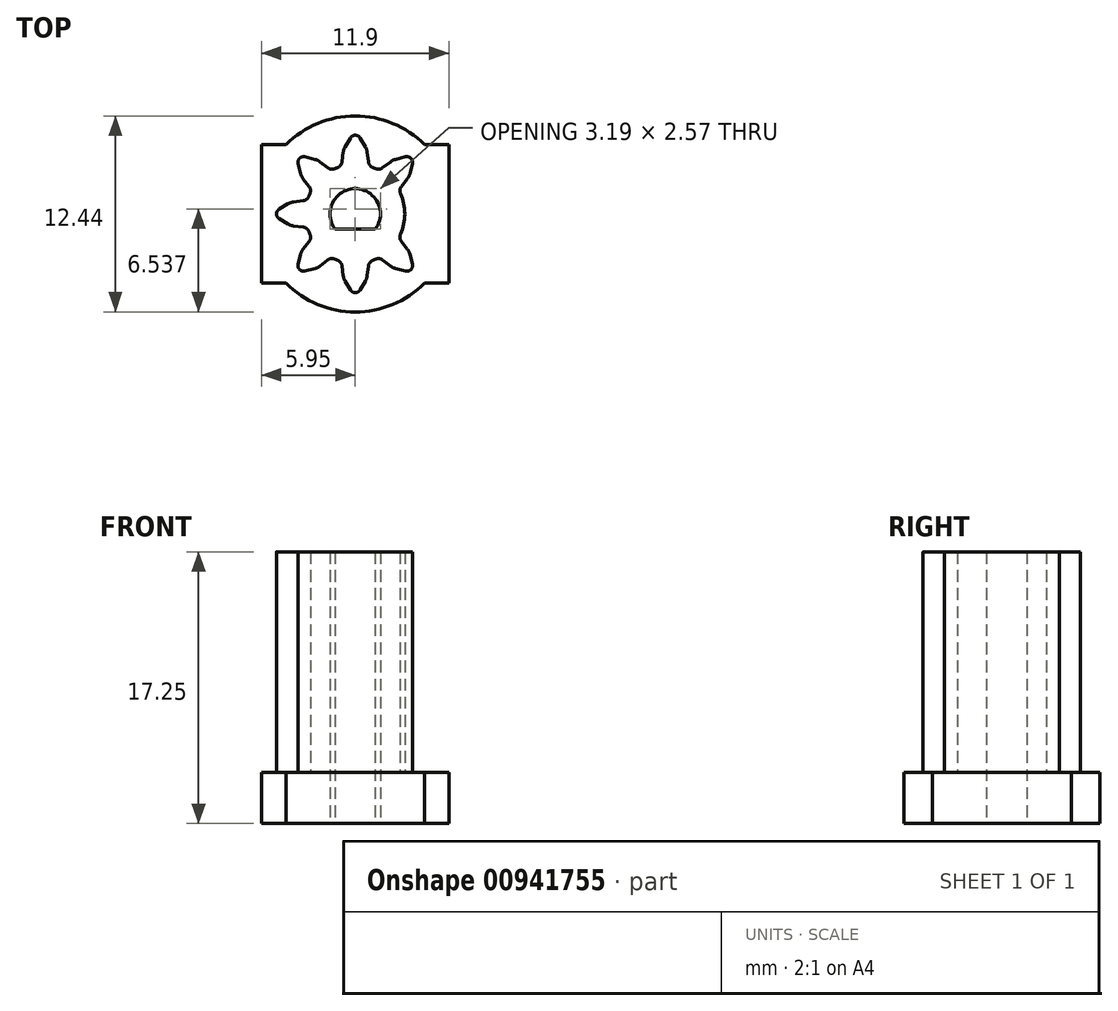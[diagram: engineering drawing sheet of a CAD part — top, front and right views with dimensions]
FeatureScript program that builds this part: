
annotation { "Feature Type Name" : "Feature", "Feature Type Description" : "" }
export const myFeature = defineFeature(function(context is Context, id is Id, definition is map)
    precondition{}
    {
        {
            var Q0;
            Q0=qCreatedBy(makeId("Top.planeOp"),FACE);
            var sketch = newSketch(context, id + "F0", { "sketchPlane" : qUnion([Q0])});
            skCircle(sketch, "E0", {"center": v(0, 0) * mm, "radius": 1.6 * mm});
            skCircle(sketch, "E1", {"center": v(0, 0) * mm, "radius": 2.55 * mm});
            skArc(sketch, "E2", {"start": v(-4.4, -4.4) * mm, "mid": v(0, -6.22) * mm, "end": v(4.4, -4.4) * mm});
            skCircle(sketch, "E3", {"center": v(0, 0) * mm, "radius": 3.15 * mm});
            skCircle(sketch, "E4", {"center": v(0, 0) * mm, "radius": 5 * mm});
            skLineSegment(sketch, "E5.bottom", {"start": v(-5.95, 4.4) * mm, "end": v(-4.4, 4.4) * mm});
            skLineSegment(sketch, "E5.top", {"start": v(-5.95, -4.4) * mm, "end": v(-4.4, -4.4) * mm});
            skLineSegment(sketch, "E5.left", {"start": v(-5.95, 4.4) * mm, "end": v(-5.95, -4.4) * mm});
            skLineSegment(sketch, "E5.right", {"start": v(5.95, 4.4) * mm, "end": v(5.95, -4.4) * mm});
            skArc(sketch, "E6.trimOffspring", {"start": v(4.4, 4.4) * mm, "mid": v(0, 6.22) * mm, "end": v(-4.4, 4.4) * mm});
            skLineSegment(sketch, "E7.trimOffspring", {"start": v(4.4, 4.4) * mm, "end": v(5.95, 4.4) * mm});
            skLineSegment(sketch, "E8.trimOffspring", {"start": v(4.4, -4.4) * mm, "end": v(5.95, -4.4) * mm});
            skLineSegment(sketch, "E9", {"start": v(0, 6.22) * mm, "end": v(0, -6.22) * mm, "construction": true});
            skLineSegment(sketch, "E10", {"start": v(-1.27, -0.97) * mm, "end": v(1.27, -0.97) * mm});
            skSolve(sketch);
        }
        {
            var Q0;
            Q0=makeQuery(id+"F0.imprint","IMPRINT",FACE,{"disambiguationData":[TD([[makeQuery(id+"F0.imprint","IMPRINT",EDGE,{"derivedFrom":sQuery(id+"F0.wireOp",EDGE,"E2")}),1.0]])]});
            var Q1;
            Q1=makeQuery(id+"F0.imprint","IMPRINT",FACE,{"disambiguationData":[TD([[makeQuery(id+"F0.imprint","IMPRINT",EDGE,{"derivedFrom":sQuery(id+"F0.wireOp",EDGE,"E3")}),-1.0]])]});
            var Q2;
            Q2=makeQuery(id+"F0.imprint","IMPRINT",FACE,{"disambiguationData":[TD([[makeQuery(id+"F0.imprint","IMPRINT",EDGE,{"derivedFrom":sQuery(id+"F0.wireOp",EDGE,"E0")}),-1.0]])]});
            var Q3;
            Q3=makeQuery(id+"F0.imprint","IMPRINT",FACE,{"disambiguationData":[TD([[makeQuery(id+"F0.imprint","IMPRINT",EDGE,{"derivedFrom":sQuery(id+"F0.wireOp",EDGE,"E1")}),-1.0]])]});
            var Q4;
            {var subQ0=sQuery(id+"F0.wireOp",EDGE,"Gm9W4LpN-Av9A-MbCA-gdo4-SThQoX5Y8GiM");Q4=makeQuery(id+"F0.imprint","IMPRINT",FACE,{"disambiguationData":[TD([[makeQuery(id+"F0.imprint","IMPRINT",EDGE,{"derivedFrom":subQ0}),-1.0]])]});}
            var Q5;
            {var subQ0=sQuery(id+"F0.wireOp",EDGE,"E10");Q5=makeQuery(id+"F0.imprint","IMPRINT",FACE,{"disambiguationData":[TD([[makeQuery(id+"F0.imprint","IMPRINT",EDGE,{"derivedFrom":subQ0}),-1.0]])]});}
            extrude(context, id + "F1", {"entities" : qUnion([Q0, Q1, Q2, Q3, Q4, Q5]), "depth" : 3.25 * mm, "offsetDistance" : 25 * mm});
        }
        {
            var Q0;
            Q0=makeQuery(id+"F1.opExtrude","CAP_FACE",FACE,{"disambiguationData":[OSD([sQuery(id+"F0.wireOp",EDGE,"E0"),sQuery(id+"F0.wireOp",EDGE,"E2"),sQuery(id+"F0.wireOp",EDGE,"E5.bottom"),sQuery(id+"F0.wireOp",EDGE,"E5.top"),sQuery(id+"F0.wireOp",EDGE,"E5.left"),sQuery(id+"F0.wireOp",EDGE,"E5.right"),sQuery(id+"F0.wireOp",EDGE,"E6.trimOffspring"),sQuery(id+"F0.wireOp",EDGE,"E7.trimOffspring"),sQuery(id+"F0.wireOp",EDGE,"E8.trimOffspring")])],"isStart":false});
            var sketch = newSketch(context, id + "F2", { "sketchPlane" : qUnion([Q0])});
            skCircle(sketch, "E11.0", {"center": v(0, 0) * mm, "radius": 5 * mm});
            skCircle(sketch, "E12.0", {"center": v(0, 0) * mm, "radius": 3.15 * mm});
            skCircle(sketch, "E13.0", {"center": v(0, 0) * mm, "radius": 2.55 * mm});
            skArc(sketch, "E14", {"start": v(4.83, -0.3) * mm, "mid": v(5, 0) * mm, "end": v(4.83, 0.3) * mm});
            skArc(sketch, "E15", {"start": v(3.31, -0.84) * mm, "mid": v(3.09, -0.93) * mm, "end": v(2.94, -1.13) * mm});
            skLineSegment(sketch, "E16", {"start": v(4.26, -0.64) * mm, "end": v(4.83, -0.3) * mm});
            skLineSegment(sketch, "E17", {"start": v(4.83, 0.3) * mm, "end": v(4.26, 0.64) * mm});
            skLineSegment(sketch, "E18", {"start": v(0, 0) * mm, "end": v(5.95, 0) * mm, "construction": true});
            skCircle(sketch, "E19.0", {"center": v(0, 0) * mm, "radius": 4.06 * mm, "construction": true});
            skArc(sketch, "E20", {"start": v(3.91, -0.76) * mm, "mid": v(4.1, -0.72) * mm, "end": v(4.26, -0.64) * mm});
            skLineSegment(sketch, "E21", {"start": v(3.91, -0.76) * mm, "end": v(3.31, -0.84) * mm});
            skArc(sketch, "E22.MirrorCS", {"start": v(3.91, 0.76) * mm, "mid": v(4.1, 0.72) * mm, "end": v(4.26, 0.64) * mm});
            skLineSegment(sketch, "E23.MirrorCS", {"start": v(3.91, 0.76) * mm, "end": v(3.31, 0.84) * mm});
            skArc(sketch, "E24.MirrorCS", {"start": v(3.31, 0.84) * mm, "mid": v(3.09, 0.93) * mm, "end": v(2.94, 1.13) * mm});
            skArc(sketch, "E25.1.0", {"start": v(1.75, -2.93) * mm, "mid": v(1.53, -2.84) * mm, "end": v(1.28, -2.88) * mm});
            skLineSegment(sketch, "E25.1.1", {"start": v(2.23, -3.3) * mm, "end": v(1.75, -2.93) * mm});
            skArc(sketch, "E25.1.2", {"start": v(2.23, -3.3) * mm, "mid": v(2.38, -3.4) * mm, "end": v(2.56, -3.47) * mm});
            skLineSegment(sketch, "E25.1.3", {"start": v(2.56, -3.47) * mm, "end": v(3.2, -3.63) * mm});
            skArc(sketch, "E25.1.4", {"start": v(3.2, -3.63) * mm, "mid": v(3.54, -3.54) * mm, "end": v(3.63, -3.2) * mm});
            skLineSegment(sketch, "E25.1.5", {"start": v(3.63, -3.2) * mm, "end": v(3.47, -2.56) * mm});
            skArc(sketch, "E25.1.6", {"start": v(3.3, -2.23) * mm, "mid": v(3.4, -2.38) * mm, "end": v(3.47, -2.56) * mm});
            skLineSegment(sketch, "E25.1.7", {"start": v(3.3, -2.23) * mm, "end": v(2.93, -1.75) * mm});
            skArc(sketch, "E25.1.8", {"start": v(2.93, -1.75) * mm, "mid": v(2.84, -1.53) * mm, "end": v(2.88, -1.28) * mm});
            skArc(sketch, "E25.2.0", {"start": v(-0.84, -3.31) * mm, "mid": v(-0.93, -3.09) * mm, "end": v(-1.12, -2.94) * mm});
            skLineSegment(sketch, "E25.2.1", {"start": v(-0.76, -3.91) * mm, "end": v(-0.84, -3.31) * mm});
            skArc(sketch, "E25.2.2", {"start": v(-0.76, -3.91) * mm, "mid": v(-0.72, -4.1) * mm, "end": v(-0.64, -4.26) * mm});
            skLineSegment(sketch, "E25.2.3", {"start": v(-0.64, -4.26) * mm, "end": v(-0.3, -4.83) * mm});
            skArc(sketch, "E25.2.4", {"start": v(-0.3, -4.83) * mm, "mid": v(0, -5) * mm, "end": v(0.3, -4.83) * mm});
            skLineSegment(sketch, "E25.2.5", {"start": v(0.3, -4.83) * mm, "end": v(0.64, -4.26) * mm});
            skArc(sketch, "E25.2.6", {"start": v(0.76, -3.91) * mm, "mid": v(0.72, -4.1) * mm, "end": v(0.64, -4.26) * mm});
            skLineSegment(sketch, "E25.2.7", {"start": v(0.76, -3.91) * mm, "end": v(0.84, -3.31) * mm});
            skArc(sketch, "E25.2.8", {"start": v(0.84, -3.31) * mm, "mid": v(0.93, -3.09) * mm, "end": v(1.13, -2.94) * mm});
            skArc(sketch, "E25.3.0", {"start": v(-2.93, -1.75) * mm, "mid": v(-2.84, -1.53) * mm, "end": v(-2.88, -1.28) * mm});
            skLineSegment(sketch, "E25.3.1", {"start": v(-3.3, -2.23) * mm, "end": v(-2.93, -1.75) * mm});
            skArc(sketch, "E25.3.2", {"start": v(-3.3, -2.23) * mm, "mid": v(-3.4, -2.38) * mm, "end": v(-3.47, -2.56) * mm});
            skLineSegment(sketch, "E25.3.3", {"start": v(-3.47, -2.56) * mm, "end": v(-3.63, -3.2) * mm});
            skArc(sketch, "E25.3.4", {"start": v(-3.63, -3.2) * mm, "mid": v(-3.54, -3.54) * mm, "end": v(-3.2, -3.63) * mm});
            skLineSegment(sketch, "E25.3.5", {"start": v(-3.2, -3.63) * mm, "end": v(-2.56, -3.47) * mm});
            skArc(sketch, "E25.3.6", {"start": v(-2.23, -3.3) * mm, "mid": v(-2.38, -3.4) * mm, "end": v(-2.56, -3.47) * mm});
            skLineSegment(sketch, "E25.3.7", {"start": v(-2.23, -3.3) * mm, "end": v(-1.75, -2.93) * mm});
            skArc(sketch, "E25.3.8", {"start": v(-1.75, -2.93) * mm, "mid": v(-1.53, -2.84) * mm, "end": v(-1.28, -2.88) * mm});
            skArc(sketch, "E25.4.0", {"start": v(-3.31, 0.84) * mm, "mid": v(-3.09, 0.93) * mm, "end": v(-2.94, 1.12) * mm});
            skLineSegment(sketch, "E25.4.1", {"start": v(-3.91, 0.76) * mm, "end": v(-3.31, 0.84) * mm});
            skArc(sketch, "E25.4.2", {"start": v(-3.91, 0.76) * mm, "mid": v(-4.1, 0.72) * mm, "end": v(-4.26, 0.64) * mm});
            skLineSegment(sketch, "E25.4.3", {"start": v(-4.26, 0.64) * mm, "end": v(-4.83, 0.3) * mm});
            skArc(sketch, "E25.4.4", {"start": v(-4.83, 0.3) * mm, "mid": v(-5, 0) * mm, "end": v(-4.83, -0.3) * mm});
            skLineSegment(sketch, "E25.4.5", {"start": v(-4.83, -0.3) * mm, "end": v(-4.26, -0.64) * mm});
            skArc(sketch, "E25.4.6", {"start": v(-3.91, -0.76) * mm, "mid": v(-4.1, -0.72) * mm, "end": v(-4.26, -0.64) * mm});
            skLineSegment(sketch, "E25.4.7", {"start": v(-3.91, -0.76) * mm, "end": v(-3.31, -0.84) * mm});
            skArc(sketch, "E25.4.8", {"start": v(-3.31, -0.84) * mm, "mid": v(-3.09, -0.93) * mm, "end": v(-2.94, -1.13) * mm});
            skArc(sketch, "E25.5.0", {"start": v(-1.75, 2.93) * mm, "mid": v(-1.53, 2.84) * mm, "end": v(-1.28, 2.88) * mm});
            skLineSegment(sketch, "E25.5.1", {"start": v(-2.23, 3.3) * mm, "end": v(-1.75, 2.93) * mm});
            skArc(sketch, "E25.5.2", {"start": v(-2.23, 3.3) * mm, "mid": v(-2.38, 3.4) * mm, "end": v(-2.56, 3.47) * mm});
            skLineSegment(sketch, "E25.5.3", {"start": v(-2.56, 3.47) * mm, "end": v(-3.2, 3.63) * mm});
            skArc(sketch, "E25.5.4", {"start": v(-3.2, 3.63) * mm, "mid": v(-3.54, 3.54) * mm, "end": v(-3.63, 3.2) * mm});
            skLineSegment(sketch, "E25.5.5", {"start": v(-3.63, 3.2) * mm, "end": v(-3.47, 2.56) * mm});
            skArc(sketch, "E25.5.6", {"start": v(-3.3, 2.23) * mm, "mid": v(-3.4, 2.38) * mm, "end": v(-3.47, 2.56) * mm});
            skLineSegment(sketch, "E25.5.7", {"start": v(-3.3, 2.23) * mm, "end": v(-2.93, 1.75) * mm});
            skArc(sketch, "E25.5.8", {"start": v(-2.93, 1.75) * mm, "mid": v(-2.84, 1.53) * mm, "end": v(-2.88, 1.28) * mm});
            skArc(sketch, "E25.6.0", {"start": v(0.84, 3.31) * mm, "mid": v(0.93, 3.09) * mm, "end": v(1.12, 2.94) * mm});
            skLineSegment(sketch, "E25.6.1", {"start": v(0.76, 3.91) * mm, "end": v(0.84, 3.31) * mm});
            skArc(sketch, "E25.6.2", {"start": v(0.76, 3.91) * mm, "mid": v(0.72, 4.1) * mm, "end": v(0.64, 4.26) * mm});
            skLineSegment(sketch, "E25.6.3", {"start": v(0.64, 4.26) * mm, "end": v(0.3, 4.83) * mm});
            skArc(sketch, "E25.6.4", {"start": v(0.3, 4.83) * mm, "mid": v(0, 5) * mm, "end": v(-0.3, 4.83) * mm});
            skLineSegment(sketch, "E25.6.5", {"start": v(-0.3, 4.83) * mm, "end": v(-0.64, 4.26) * mm});
            skArc(sketch, "E25.6.6", {"start": v(-0.76, 3.91) * mm, "mid": v(-0.72, 4.1) * mm, "end": v(-0.64, 4.26) * mm});
            skLineSegment(sketch, "E25.6.7", {"start": v(-0.76, 3.91) * mm, "end": v(-0.84, 3.31) * mm});
            skArc(sketch, "E25.6.8", {"start": v(-0.84, 3.31) * mm, "mid": v(-0.93, 3.09) * mm, "end": v(-1.13, 2.94) * mm});
            skArc(sketch, "E26.0.7.0", {"start": v(2.93, 1.75) * mm, "mid": v(2.84, 1.53) * mm, "end": v(2.88, 1.28) * mm});
            skLineSegment(sketch, "E26.4.7.0", {"start": v(3.3, 2.23) * mm, "end": v(2.93, 1.75) * mm});
            skArc(sketch, "E26.7.7.0", {"start": v(3.3, 2.23) * mm, "mid": v(3.4, 2.38) * mm, "end": v(3.47, 2.56) * mm});
            skLineSegment(sketch, "E26.11.7.0", {"start": v(3.47, 2.56) * mm, "end": v(3.63, 3.2) * mm});
            skArc(sketch, "E26.14.7.0", {"start": v(3.63, 3.2) * mm, "mid": v(3.54, 3.54) * mm, "end": v(3.2, 3.63) * mm});
            skLineSegment(sketch, "E26.18.7.0", {"start": v(3.2, 3.63) * mm, "end": v(2.56, 3.47) * mm});
            skArc(sketch, "E26.21.7.0", {"start": v(2.23, 3.3) * mm, "mid": v(2.38, 3.4) * mm, "end": v(2.56, 3.47) * mm});
            skLineSegment(sketch, "E26.25.7.0", {"start": v(2.23, 3.3) * mm, "end": v(1.75, 2.93) * mm});
            skArc(sketch, "E26.28.7.0", {"start": v(1.75, 2.93) * mm, "mid": v(1.53, 2.84) * mm, "end": v(1.28, 2.88) * mm});
            skArc(sketch, "E26.0.8.0", {"start": v(3.31, -0.84) * mm, "mid": v(3.09, -0.93) * mm, "end": v(2.94, -1.12) * mm});
            skSolve(sketch);
        }
        {
            var Q0;
            {var subQ1=sQuery(id+"F2.wireOp",EDGE,"E25.4.0");Q0=makeQuery(id+"F2.imprint","IMPRINT",FACE,{"disambiguationData":[TD([[makeQuery(id+"F2.imprint","IMPRINT",EDGE,{"derivedFrom":subQ1}),-1.0]])]});}
            var Q1;
            {var subQ4=sQuery(id+"F2.wireOp",EDGE,"E25.5.0");Q1=makeQuery(id+"F2.imprint","IMPRINT",FACE,{"disambiguationData":[TD([[makeQuery(id+"F2.imprint","IMPRINT",EDGE,{"derivedFrom":subQ4}),-1.0]])]});}
            var Q2;
            {var subQ3=sQuery(id+"F2.wireOp",EDGE,"E25.6.0");Q2=makeQuery(id+"F2.imprint","IMPRINT",FACE,{"disambiguationData":[TD([[makeQuery(id+"F2.imprint","IMPRINT",EDGE,{"derivedFrom":subQ3}),-1.0]])]});}
            var Q3;
            {var subQ0=sQuery(id+"F2.wireOp",EDGE,"E25.7.0");Q3=makeQuery(id+"F2.imprint","IMPRINT",FACE,{"disambiguationData":[TD([[makeQuery(id+"F2.imprint","IMPRINT",EDGE,{"derivedFrom":subQ0}),-1.0]])]});}
            var Q4;
            {var subQ4=sQuery(id+"F2.wireOp",EDGE,"E25.1.0");Q4=makeQuery(id+"F2.imprint","IMPRINT",FACE,{"disambiguationData":[TD([[makeQuery(id+"F2.imprint","IMPRINT",EDGE,{"derivedFrom":subQ4}),-1.0]])]});}
            var Q5;
            {var subQ0=sQuery(id+"F2.wireOp",EDGE,"E25.2.0");Q5=makeQuery(id+"F2.imprint","IMPRINT",FACE,{"disambiguationData":[TD([[makeQuery(id+"F2.imprint","IMPRINT",EDGE,{"derivedFrom":subQ0}),-1.0]])]});}
            var Q6;
            {var subQ4=sQuery(id+"F2.wireOp",EDGE,"E25.3.0");Q6=makeQuery(id+"F2.imprint","IMPRINT",FACE,{"disambiguationData":[TD([[makeQuery(id+"F2.imprint","IMPRINT",EDGE,{"derivedFrom":subQ4}),-1.0]])]});}
            var Q7;
            Q7=makeQuery(id+"F2.imprint","IMPRINT",FACE,{"disambiguationData":[TD([[makeQuery(id+"F2.imprint","IMPRINT",EDGE,{"derivedFrom":sQuery(id+"F2.wireOp",EDGE,"E13.0")}),-1.0]])]});
            var Q8;
            Q8=makeQuery(id+"F2.imprint","IMPRINT",FACE,{"disambiguationData":[TD([[makeQuery(id+"F2.imprint","IMPRINT",EDGE,{"derivedFrom":sQuery(id+"F2.wireOp",EDGE,"E13.0")}),1.0]])]});
            var Q9;
            {var subQ4=sQuery(id+"F2.wireOp",EDGE,"E26.0.7.0");Q9=makeQuery(id+"F2.imprint","IMPRINT",FACE,{"disambiguationData":[TD([[makeQuery(id+"F2.imprint","IMPRINT",EDGE,{"derivedFrom":subQ4}),-1.0]])]});}
            var Q10;
            {var subQ4=sQuery(id+"F2.wireOp",EDGE,"E26.0.8.0");Q10=makeQuery(id+"F2.imprint","IMPRINT",FACE,{"disambiguationData":[TD([[makeQuery(id+"F2.imprint","IMPRINT",EDGE,{"derivedFrom":subQ4}),-1.0]])]});}
            extrude(context, id + "F3", {"entities" : qUnion([Q0, Q1, Q2, Q3, Q4, Q5, Q6, Q7, Q8, Q9, Q10]), "operationType" : NewBodyOperationType.ADD, "depth" : 14 * mm, "offsetDistance" : 25 * mm});
        }
    });
